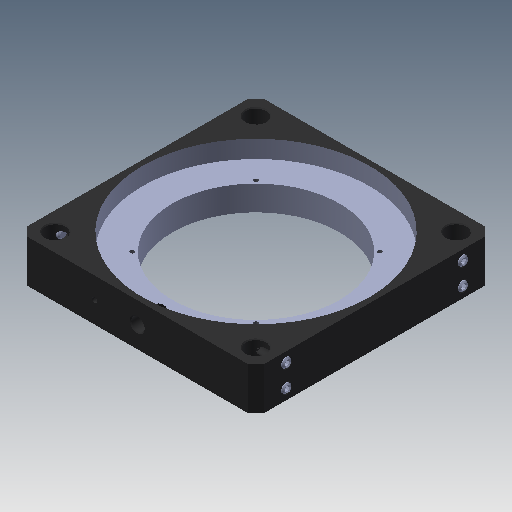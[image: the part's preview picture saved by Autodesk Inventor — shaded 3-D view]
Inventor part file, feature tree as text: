
AUTODESK INVENTOR PART (.ipt)
format: ipt  version: 2019 (Build 230136000, 136)  size: 411,136 bytes
history: native  units: mm
features: other x10, imported_body x9, sketch x3, extrude x2, projected_geometry x2, hole x1
ambient origin geometry x8: Origin, YZ Plane, XZ Plane, XY Plane, X Axis, Y Axis, Z Axis, Center Point
bodies: Body1 (feature_tree), Body2 (feature_tree), Body3 (feature_tree), Body4 (feature_tree), Body5 (feature_tree), Body6 (feature_tree), Body7 (feature_tree), Body8 (feature_tree), Body9 (feature_tree)
feature tree (27):
  other  "13108-001-1-solid1"
  other  "13108-E0W1"
  extrude  "Extrusion1"  Depth=5.25mm TaperAngle=0.0deg
  extrude  "Extrusion2"  Depth=4.0mm TaperAngle=0.0deg
  hole  "Hole1"  [1 undecoded]
  other  "SS4S019-1-1-solid1"
  other  "SS4S019-1-2-solid1"
  other  "SS4S019-1-3-solid1"
  other  "SS4S019-1-4-solid1"
  other  "SS4S019-1-5-solid1"
  other  "SS4S019-1-6-solid1"
  other  "SS4S019-1-7-solid1"
  other  "SS4S019-1-8-solid1"
  imported_body  "Base1"
  imported_body  "Base2"
  imported_body  "Base3"
  imported_body  "Base4"
  imported_body  "Base5"
  imported_body  "Base6"
  imported_body  "Base7"
  imported_body  "Base8"
  imported_body  "Base9"
  sketch  "Sketch1"  dims[d1=68.0mm d2=5.25mm d3=0.0mm]
  projected_geometry  "Projected Loop1"
  sketch  "Sketch2"  dims[d4=50.0mm d5=4.0mm d6=0.0mm]
  sketch  "Sketch3"  dims[d7=36.99764mm d8=36.99764mm d9=1.3208mm d10=3.4036mm d11=9.525mm d12=6.35mm d13=14.3117mm d14=5.5118mm d15=20.594885mm]
  projected_geometry  "Projected Loop2"
note: 1 required parameter value undecoded (feature->parameter linkage not recoverable at this tier; creation-order binding heuristic only, values carry confidence <= 0.55)
